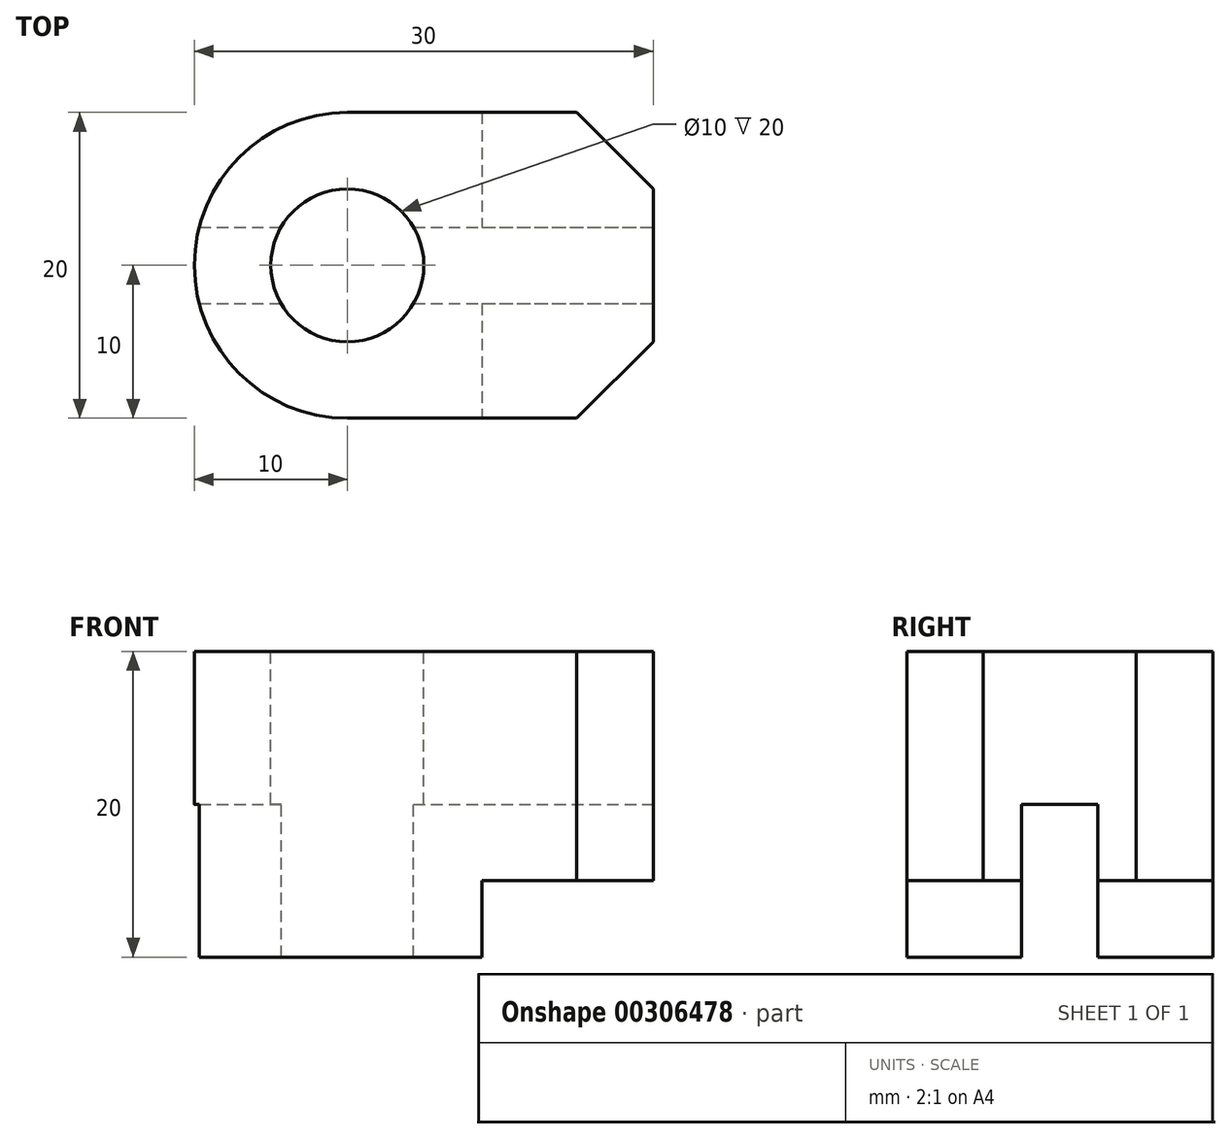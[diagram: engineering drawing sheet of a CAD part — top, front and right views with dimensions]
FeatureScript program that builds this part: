
annotation { "Feature Type Name" : "Feature", "Feature Type Description" : "" }
export const myFeature = defineFeature(function(context is Context, id is Id, definition is map)
    precondition{}
    {
        {
            var Q0;
            Q0=qCreatedBy(makeId("Front.planeOp"),FACE);
            var sketch = newSketch(context, id + "F0", { "sketchPlane" : qUnion([Q0])});
            skLineSegment(sketch, "E0", {"start": v(0, 0) * mm, "end": v(0, 20) * mm});
            skLineSegment(sketch, "E1", {"start": v(0, 20) * mm, "end": v(30, 20) * mm});
            skLineSegment(sketch, "E2", {"start": v(30, 20) * mm, "end": v(30, 5) * mm});
            skLineSegment(sketch, "E3", {"start": v(18.78, 0) * mm, "end": v(0, 0) * mm});
            skLineSegment(sketch, "E4", {"start": v(10, 5) * mm, "end": v(30, 5) * mm});
            skLineSegment(sketch, "E5", {"start": v(18.78, 0) * mm, "end": v(18.78, 5) * mm});
            skSolve(sketch);
        }
        {
            var Q0;
            Q0=makeQuery(id+"F0.imprint","IMPRINT",FACE,{"disambiguationData":[TD([[makeQuery(id+"F0.imprint","IMPRINT",EDGE,{"derivedFrom":sQuery(id+"F0.wireOp",EDGE,"E0")}),-1.0]])]});
            extrude(context, id + "F1", {"entities" : qUnion([Q0]), "oppositeDirection" : true, "depth" : 20 * mm});
        }
        {
            var Q0;
            Q0=makeQuery(id+"F1.opExtrude","SWEPT_FACE",FACE,{"disambiguationData":[OSD([sQuery(id+"F0.wireOp",EDGE,"E1")])]});
            var sketch = newSketch(context, id + "F2", { "sketchPlane" : qUnion([Q0])});
            skLineSegment(sketch, "E6", {"start": v(0, 10) * mm, "end": v(56.2, 10) * mm, "construction": true});
            skCircle(sketch, "E7", {"center": v(10, 10) * mm, "radius": 10 * mm});
            skCircle(sketch, "E8", {"center": v(10, 10) * mm, "radius": 5 * mm});
            skLineSegment(sketch, "E9", {"start": v(25, 20) * mm, "end": v(30, 15) * mm});
            skLineSegment(sketch, "E10", {"start": v(30, 15) * mm, "end": v(30, 20) * mm});
            skLineSegment(sketch, "E11", {"start": v(30, 20) * mm, "end": v(25, 20) * mm});
            skLineSegment(sketch, "E12.MirrorCS", {"start": v(25, 0) * mm, "end": v(30, 5) * mm});
            skLineSegment(sketch, "E13.MirrorCS", {"start": v(30, 0) * mm, "end": v(25, 0) * mm});
            skLineSegment(sketch, "E14.MirrorCS", {"start": v(30, 5) * mm, "end": v(30, 0) * mm});
            skSolve(sketch);
        }
        {
            var Q0;
            {var subQ0=sQuery(id+"F2.wireOp",EDGE,"E7");var subQ1=sQuery(id+"F0.wireOp",EDGE,"E1");var subQ4=makeQuery(id+"F1.opExtrude","CAP_EDGE",EDGE,{"disambiguationData":[OSD([subQ1])],"isStart":false});var subQ5=makeQuery(id+"F2.imprint","INTERSECT",VERTEX,{"derivedFrom":[subQ4,subQ0]});Q0=makeQuery(id+"F2.imprint","IMPRINT",FACE,{"disambiguationData":[TD([[makeQuery(id+"F2.imprint","IMPRINT",EDGE,{"disambiguationData":[TD([[subQ5,-1.0]])],"derivedFrom":subQ0}),-1.0]])]});}
            extrude(context, id + "F3", {"entities" : qUnion([Q0]), "operationType" : NewBodyOperationType.REMOVE, "oppositeDirection" : true, "depth" : 25 * mm});
        }
        {
            var Q0;
            {var subQ0=sQuery(id+"F2.wireOp",EDGE,"E7");var subQ1=sQuery(id+"F0.wireOp",EDGE,"E1");var subQ4=makeQuery(id+"F1.opExtrude","CAP_EDGE",EDGE,{"disambiguationData":[OSD([subQ1])],"isStart":true});var subQ5=makeQuery(id+"F2.imprint","INTERSECT",VERTEX,{"derivedFrom":[subQ4,subQ0]});Q0=makeQuery(id+"F2.imprint","IMPRINT",FACE,{"disambiguationData":[TD([[makeQuery(id+"F2.imprint","IMPRINT",EDGE,{"disambiguationData":[TD([[subQ5,1.0]])],"derivedFrom":subQ0}),-1.0]])]});}
            extrude(context, id + "F4", {"entities" : qUnion([Q0]), "operationType" : NewBodyOperationType.REMOVE, "oppositeDirection" : true, "depth" : 25 * mm});
        }
        {
            var Q0;
            Q0=makeQuery(id+"F1.opExtrude","SWEPT_FACE",FACE,{"disambiguationData":[OSD([sQuery(id+"F0.wireOp",EDGE,"E2")])]});
            var sketch = newSketch(context, id + "F5", { "sketchPlane" : qUnion([Q0])});
            skLineSegment(sketch, "E15", {"start": v(10, 20) * mm, "end": v(10, -7.78) * mm, "construction": true});
            skPoint(sketch, "E15.endSnap0", {"position": v(10, 5) * mm});
            skLineSegment(sketch, "E16.bottom", {"start": v(7.5, 0) * mm, "end": v(12.5, 0) * mm});
            skLineSegment(sketch, "E16.top", {"start": v(7.5, 10) * mm, "end": v(12.5, 10) * mm});
            skLineSegment(sketch, "E16.left", {"start": v(7.5, 0) * mm, "end": v(7.5, 10) * mm});
            skLineSegment(sketch, "E16.right", {"start": v(12.5, 0) * mm, "end": v(12.5, 10) * mm});
            skSolve(sketch);
        }
        {
            var Q0;
            Q0=makeQuery(id+"F2.imprint","IMPRINT",FACE,{"disambiguationData":[TD([[makeQuery(id+"F2.imprint","IMPRINT",EDGE,{"derivedFrom":sQuery(id+"F2.wireOp",EDGE,"E9")}),1.0]])]});
            extrude(context, id + "F6", {"entities" : qUnion([Q0]), "operationType" : NewBodyOperationType.REMOVE, "oppositeDirection" : true, "depth" : 25 * mm});
        }
        {
            var Q0;
            Q0=makeQuery(id+"F2.imprint","IMPRINT",FACE,{"disambiguationData":[TD([[makeQuery(id+"F2.imprint","IMPRINT",EDGE,{"derivedFrom":sQuery(id+"F2.wireOp",EDGE,"E12.MirrorCS")}),-1.0]])]});
            extrude(context, id + "F7", {"entities" : qUnion([Q0]), "operationType" : NewBodyOperationType.REMOVE, "oppositeDirection" : true, "depth" : 25 * mm});
        }
        {
            var Q0;
            Q0=makeQuery(id+"F2.imprint","IMPRINT",FACE,{"disambiguationData":[TD([[makeQuery(id+"F2.imprint","IMPRINT",EDGE,{"derivedFrom":sQuery(id+"F2.wireOp",EDGE,"E8")}),1.0]])]});
            extrude(context, id + "F8", {"entities" : qUnion([Q0]), "operationType" : NewBodyOperationType.REMOVE, "oppositeDirection" : true, "depth" : 30 * mm});
        }
        {
            var Q0;
            {var subQ0=sQuery(id+"F5.wireOp",EDGE,"E16.top");Q0=makeQuery(id+"F5.imprint","IMPRINT",FACE,{"disambiguationData":[TD([[makeQuery(id+"F5.imprint","IMPRINT",EDGE,{"derivedFrom":subQ0}),-1.0]])]});}
            extrude(context, id + "F9", {"entities" : qUnion([Q0]), "operationType" : NewBodyOperationType.REMOVE, "oppositeDirection" : true, "depth" : 50 * mm});
        }
        {
            var Q0;
            {var subQ0=sQuery(id+"F5.wireOp",EDGE,"E16.bottom");Q0=makeQuery(id+"F5.imprint","IMPRINT",FACE,{"disambiguationData":[TD([[makeQuery(id+"F5.imprint","IMPRINT",EDGE,{"derivedFrom":subQ0}),1.0]])]});}
            extrude(context, id + "F10", {"entities" : qUnion([Q0]), "operationType" : NewBodyOperationType.REMOVE, "oppositeDirection" : true, "depth" : 50 * mm});
        }
    });
